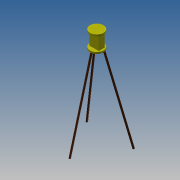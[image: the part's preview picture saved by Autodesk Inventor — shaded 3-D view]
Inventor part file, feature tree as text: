
AUTODESK INVENTOR PART (.ipt)
format: ipt  version: 2014 SP1 (Build 180222100, 222)  size: 122,880 bytes
history: native  units: in
note: dims shown in document units (in); Inventor stores cm internally (conversion verified against a paired STEP export)
features: sketch x7, extrude x5, plane x2, pattern_circular x1
ambient origin geometry x8: Origin, YZ Plane, XZ Plane, XY Plane, X Axis, Y Axis, Z Axis, Center Point
bodies: Solid1 (feature_tree)
feature tree (15):
  extrude  "Extrusion1"  Depth=1.0in TaperAngle=0.0deg
  sketch  "Sketch2"  dims[d3=2.0in d4=75.0deg]
  plane  "Work Plane1"
  sketch  "Sketch3"  dims[d5=1.5in d6=1.5in]
  plane  "Work Plane2"
  extrude  "Extrusion2"  TaperAngle=75.0deg  [1 undecoded]
  extrude  "Extrusion3"  Depth=1.5in
  pattern_circular  "Circular Pattern2"  Count=127  [1 undecoded]
  extrude  "Extrusion4"  Depth=8.0in TaperAngle=0.0deg
  extrude  "Extrusion6"  Depth=1.0in TaperAngle=0.0deg
  sketch  "Sketch1"  dims[d0=8.0in d1=1.0in d2=0.0in]
  sketch  "Sketch4"  dims[d7=1.0in d8=0.0in]
  sketch  "Sketch5"  dims[d9=1.0in d10=50.0in d11=0.0in]
  sketch  "Sketch6"  dims[d15=1.1811in d16=360.0deg d18=8.0in d19=0.0in]
  sketch  "Sketch8"  dims[d23=8.0in d24=1.0in d25=0.0in]
note: 2 required parameter values undecoded (feature->parameter linkage not recoverable at this tier; creation-order binding heuristic only, values carry confidence <= 0.55)
